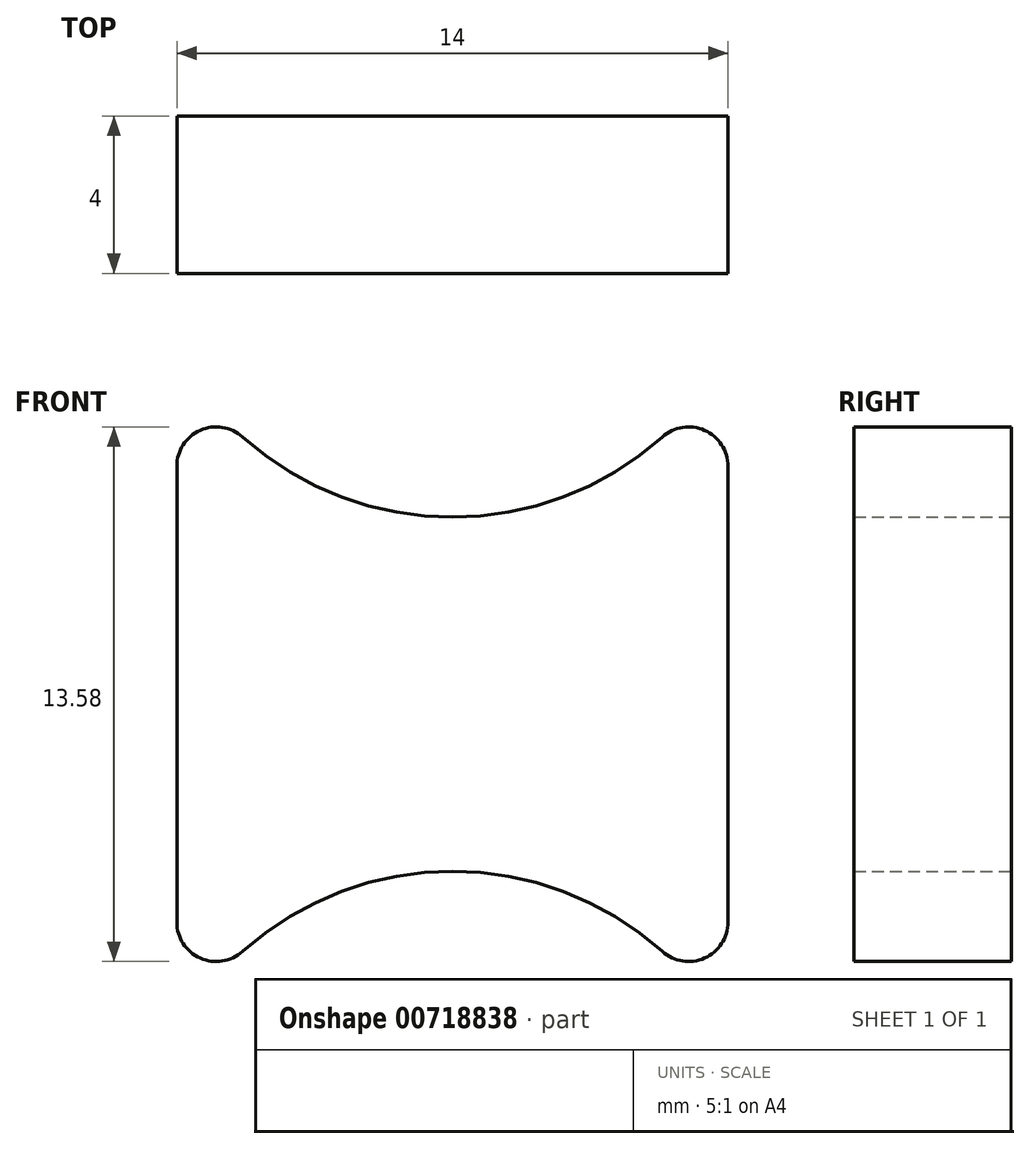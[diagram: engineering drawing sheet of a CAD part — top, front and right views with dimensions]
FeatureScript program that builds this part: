
annotation { "Feature Type Name" : "Feature", "Feature Type Description" : "" }
export const myFeature = defineFeature(function(context is Context, id is Id, definition is map)
    precondition{}
    {
        {
            var Q0;
            Q0=qCreatedBy(makeId("Front.planeOp"),FACE);
            var sketch = newSketch(context, id + "F0", { "sketchPlane" : qUnion([Q0])});
            skLineSegment(sketch, "E0.left", {"start": v(-7, 8.63) * mm, "end": v(-7, -8.63) * mm});
            skLineSegment(sketch, "E0.right", {"start": v(7, 8.63) * mm, "end": v(7, -8.63) * mm});
            skArc(sketch, "E1", {"start": v(7, -8.63) * mm, "mid": v(0, -4.5) * mm, "end": v(-7, -8.63) * mm});
            skArc(sketch, "E2.MirrorCS", {"start": v(7, 8.63) * mm, "mid": v(0, 4.5) * mm, "end": v(-7, 8.63) * mm});
            skSolve(sketch);
        }
        {
            var Q0;
            Q0=makeQuery(id+"F0.imprint","IMPRINT",FACE,{"disambiguationData":[TD([[makeQuery(id+"F0.imprint","IMPRINT",EDGE,{"derivedFrom":sQuery(id+"F0.wireOp",EDGE,"E0.left")}),1.0]])]});
            extrude(context, id + "F1", {"entities" : qUnion([Q0]), "depth" : 4 * mm, "offsetDistance" : 25 * mm});
        }
        {
            var Q0;
            Q0=makeQuery(id+"F1.opExtrude","SWEPT_EDGE",EDGE,{"disambiguationData":[OSD([sQuery(id+"F0.wireOp",EDGE,"E0.left"),sQuery(id+"F0.wireOp",EDGE,"E1")])]});
            var Q1;
            Q1=makeQuery(id+"F1.opExtrude","SWEPT_EDGE",EDGE,{"disambiguationData":[OSD([sQuery(id+"F0.wireOp",EDGE,"E0.right"),sQuery(id+"F0.wireOp",EDGE,"E1")])]});
            var Q2;
            Q2=makeQuery(id+"F1.opExtrude","SWEPT_EDGE",EDGE,{"disambiguationData":[OSD([sQuery(id+"F0.wireOp",EDGE,"E0.left"),sQuery(id+"F0.wireOp",EDGE,"E2.MirrorCS")])]});
            var Q3;
            Q3=makeQuery(id+"F1.opExtrude","SWEPT_EDGE",EDGE,{"disambiguationData":[OSD([sQuery(id+"F0.wireOp",EDGE,"E0.right"),sQuery(id+"F0.wireOp",EDGE,"E2.MirrorCS")])]});
            fillet(context, id + "F2", {"entities" : qUnion([Q0, Q1, Q2, Q3]), "radius" : 1 * mm, "tangentPropagation" : true, "allowEdgeOverflow" : false});
        }
    });
